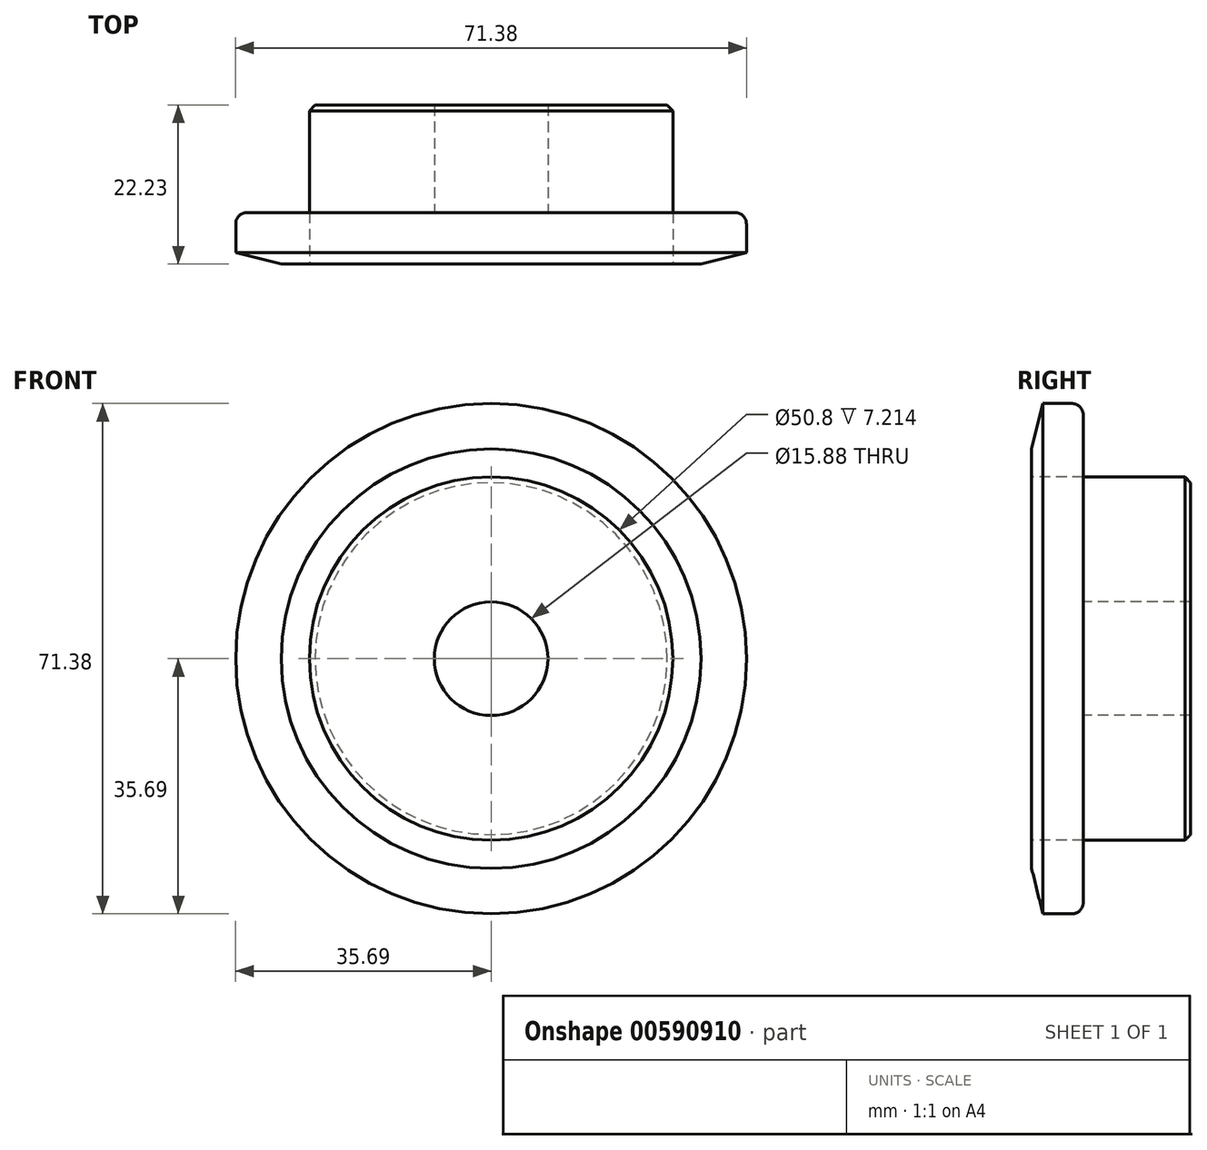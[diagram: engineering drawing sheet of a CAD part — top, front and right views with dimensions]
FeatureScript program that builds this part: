
annotation { "Feature Type Name" : "Feature", "Feature Type Description" : "" }
export const myFeature = defineFeature(function(context is Context, id is Id, definition is map)
    precondition{}
    {
        {
            var Q0;
            Q0=qCreatedBy(makeId("Right.planeOp"),FACE);
            var sketch = newSketch(context, id + "F0", { "sketchPlane" : qUnion([Q0])});
            skLineSegment(sketch, "E0", {"start": v(0, 0) * mm, "end": v(12.93, 0) * mm, "construction": true});
            skLineSegment(sketch, "E1.bottom", {"start": v(0, 7.94) * mm, "end": v(7.21, 7.94) * mm});
            skLineSegment(sketch, "E1.top", {"start": v(0, 35.69) * mm, "end": v(7.21, 35.69) * mm});
            skLineSegment(sketch, "E1.left", {"start": v(0, 7.94) * mm, "end": v(0, 35.69) * mm});
            skLineSegment(sketch, "E1.right", {"start": v(7.21, 7.94) * mm, "end": v(7.21, 35.69) * mm});
            skLineSegment(sketch, "E2.bottom", {"start": v(0, 7.94) * mm, "end": v(22.22, 7.94) * mm});
            skLineSegment(sketch, "E2.top", {"start": v(0, 25.4) * mm, "end": v(22.22, 25.4) * mm});
            skLineSegment(sketch, "E2.left", {"start": v(0, 7.94) * mm, "end": v(0, 25.4) * mm});
            skLineSegment(sketch, "E2.right", {"start": v(22.22, 7.94) * mm, "end": v(22.22, 25.4) * mm});
            skLineSegment(sketch, "E3.MirrorCS", {"start": v(0, -7.94) * mm, "end": v(7.21, -7.94) * mm});
            skLineSegment(sketch, "E4.MirrorCS", {"start": v(22.22, -7.94) * mm, "end": v(22.23, -25.4) * mm});
            skLineSegment(sketch, "E5.MirrorCS", {"start": v(0, -7.94) * mm, "end": v(0, -25.4) * mm});
            skLineSegment(sketch, "E6.MirrorCS", {"start": v(0, -35.69) * mm, "end": v(7.21, -35.69) * mm});
            skLineSegment(sketch, "E7.MirrorCS", {"start": v(0, -7.94) * mm, "end": v(0, -35.69) * mm});
            skLineSegment(sketch, "E8.MirrorCS", {"start": v(7.21, -7.94) * mm, "end": v(7.21, -35.69) * mm});
            skLineSegment(sketch, "E9.MirrorCS", {"start": v(0, -7.94) * mm, "end": v(22.22, -7.94) * mm});
            skLineSegment(sketch, "E10.MirrorCS", {"start": v(0, -25.4) * mm, "end": v(22.22, -25.4) * mm});
            skSolve(sketch);
        }
        {
            var Q0;
            {var subQ0=sQuery(id+"F0.wireOp",EDGE,"E1.top");Q0=makeQuery(id+"F0.imprint","IMPRINT",FACE,{"disambiguationData":[TD([[makeQuery(id+"F0.imprint","IMPRINT",EDGE,{"derivedFrom":subQ0}),-1.0]])]});}
            var Q1;
            {var subQ5=sQuery(id+"F0.wireOp",EDGE,"E2.left");Q1=makeQuery(id+"F0.imprint","IMPRINT",FACE,{"disambiguationData":[TD([[makeQuery(id+"F0.imprint","IMPRINT",EDGE,{"derivedFrom":subQ5}),-1.0]])]});}
            var Q2;
            {var subQ5=sQuery(id+"F0.wireOp",EDGE,"E2.right");Q2=makeQuery(id+"F0.imprint","IMPRINT",FACE,{"disambiguationData":[TD([[makeQuery(id+"F0.imprint","IMPRINT",EDGE,{"derivedFrom":subQ5}),1.0]])]});}
            var Q3;
            Q3=sQuery(id+"F0.wireOp",EDGE,"E0");
            revolve(context, id + "F1", {"entities" : qUnion([Q0, Q1, Q2]), "axis" : qUnion([Q3]), "revolveType" : RevolveType.FULL});
        }
        {
            var Q0;
            Q0=makeQuery(id+"F1.opRevolve","SWEPT_EDGE",EDGE,{"disambiguationData":[OSD([sQuery(id+"F0.wireOp",EDGE,"E1.top"),sQuery(id+"F0.wireOp",EDGE,"E1.right")])]});
            fillet(context, id + "F2", {"entities" : qUnion([Q0]), "radius" : 1.59 * mm, "tangentPropagation" : true, "allowEdgeOverflow" : false});
        }
        {
            var Q0;
            Q0=makeQuery(id+"F1.opRevolve","SWEPT_EDGE",EDGE,{"disambiguationData":[OSD([sQuery(id+"F0.wireOp",EDGE,"E2.top"),sQuery(id+"F0.wireOp",EDGE,"E2.right")])]});
            chamfer(context, id + "F3", {"entities" : qUnion([Q0]), "width" : 0.8 * mm, "tangentPropagation" : true});
        }
        {
            var Q0;
            Q0=makeQuery(id+"F1.opRevolve","SWEPT_EDGE",EDGE,{"disambiguationData":[OSD([sQuery(id+"F0.wireOp",EDGE,"E1.top"),sQuery(id+"F0.wireOp",EDGE,"E1.left")])]});
            var Q1;
            {var subQ0=sQuery(id+"F0.wireOp",EDGE,"E1.top");Q1=makeQuery(id+"F2.opFillet","BLEND_EDGE",EDGE,{"blendedFrom":[makeQuery(id+"F1.opRevolve","SWEPT_EDGE",EDGE,{"disambiguationData":[OSD([subQ0,sQuery(id+"F0.wireOp",EDGE,"E1.right")])]}),makeQuery(id+"F1.opRevolve","SWEPT_FACE",FACE,{"disambiguationData":[OSD([subQ0])]})],"blendedInto":[makeQuery(id+"F1.opRevolve","SWEPT_FACE",FACE,{"disambiguationData":[OSD([subQ0])]})]});}
            chamfer(context, id + "F4", {"entities" : qUnion([Q0, Q1]), "chamferType" : ChamferType.TWO_OFFSETS, "width1" : 6.35 * mm, "oppositeDirection" : false, "width2" : 1.57 * mm, "tangentPropagation" : true});
        }
    });
